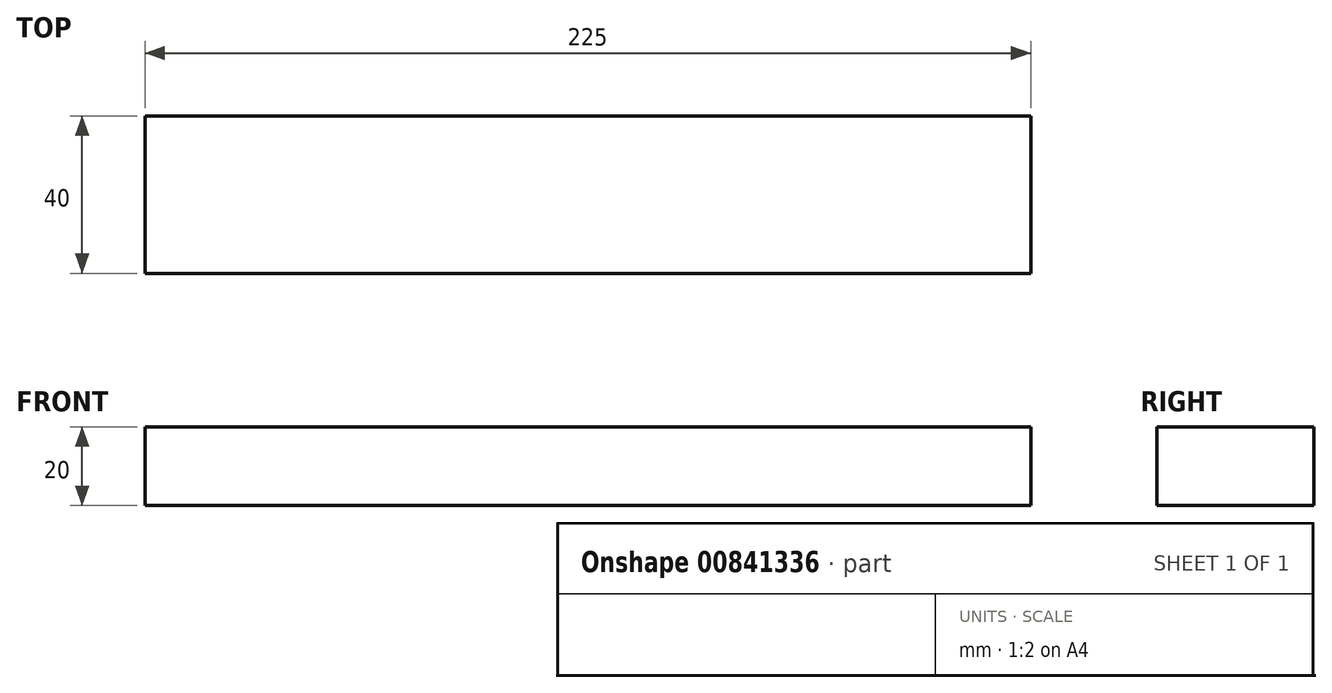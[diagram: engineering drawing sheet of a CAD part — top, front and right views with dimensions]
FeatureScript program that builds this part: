
annotation { "Feature Type Name" : "Feature", "Feature Type Description" : "" }
export const myFeature = defineFeature(function(context is Context, id is Id, definition is map)
    precondition{}
    {
        {
            var Q0;
            Q0=qCreatedBy(makeId("Right.planeOp"),FACE);
            var sketch = newSketch(context, id + "F0", { "sketchPlane" : qUnion([Q0])});
            skLineSegment(sketch, "E0.bottom", {"start": v(-20, 10) * mm, "end": v(20, 10) * mm});
            skLineSegment(sketch, "E0.top", {"start": v(-20, -10) * mm, "end": v(20, -10) * mm});
            skLineSegment(sketch, "E0.left", {"start": v(-20, 10) * mm, "end": v(-20, -10) * mm});
            skLineSegment(sketch, "E0.right", {"start": v(20, 10) * mm, "end": v(20, -10) * mm});
            skLineSegment(sketch, "E1", {"start": v(-20, 0) * mm, "end": v(20, 0) * mm});
            skSolve(sketch);
        }
        {
            var Q0;
            Q0=qSketchRegion(id+"F0",true);
            extrude(context, id + "F1", {"entities" : qUnion([Q0]), "depth" : 225 * mm, "offsetDistance" : 25 * mm});
        }
    });
